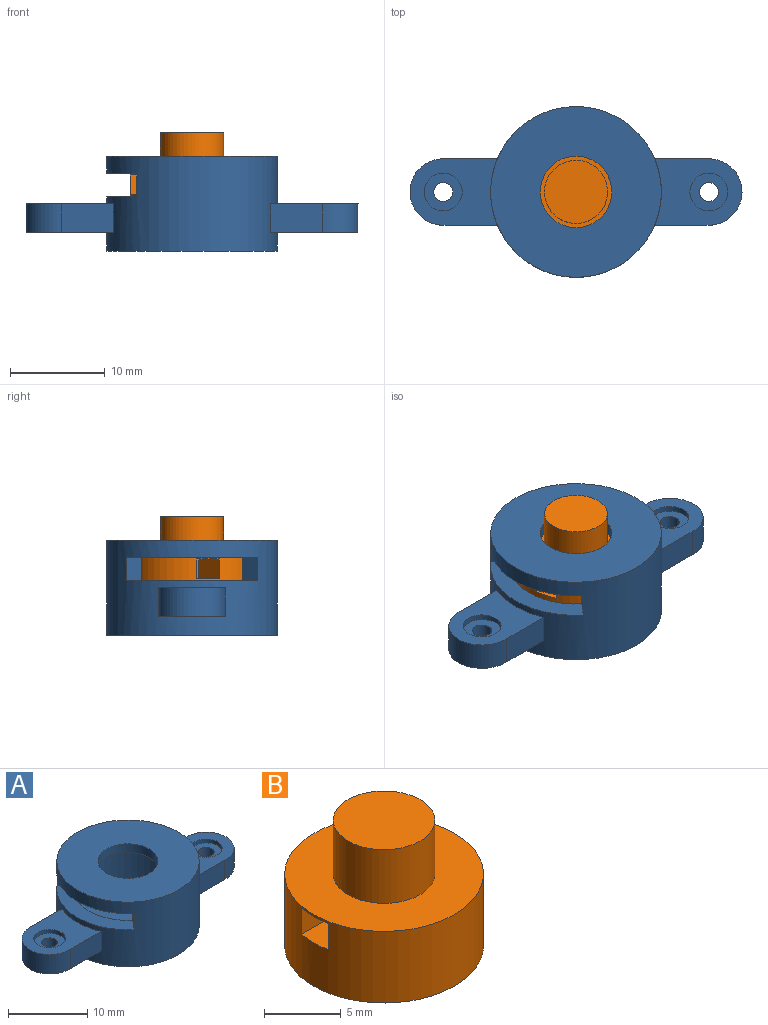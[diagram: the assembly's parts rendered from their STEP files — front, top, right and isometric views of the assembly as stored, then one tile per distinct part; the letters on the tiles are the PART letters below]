
ASSEMBLY  parts=2 mates=1
PART A: 27 faces, bbox 35x18x10 mm
  f0: cylinder r=6.95mm len=13.9mm, axis (0,0,1), area 259.3mm2, adj f5,f6,f23,f24,f25,f26
  f1: cylinder r=3.78mm len=7.55mm, axis (0,0,1), area 31.8mm2, adj f2,f6
  f2: plane 18x18mm, normal (0,0,1), area 209.7mm2, adj f1,f3
  f3: cylinder r=9mm len=18mm, axis (0,0,1), area 483.1mm2, adj f2,f4,f8,f9,f10,f11,f12,f14
  f4: plane 18x18mm, normal (0,0,-1), area 254.5mm2, adj f3
  f5: plane 13.9x13.9mm, normal (0,0,1), area 151.7mm2, adj f0
  f6: plane 13.9x13.9mm, normal (0,0,-1), area 107mm2, adj f0,f1
  f7: cylinder r=3.5mm len=7mm, axis (0,0,1), area 33.9mm2, adj f8,f9,f10,f11
  f8: plane 5.51x3mm, normal (0,-1,0), area 16.5mm2, adj f3,f7,f10,f11
  f9: plane 5.59x3mm, normal (0,1,0), area 16.8mm2, adj f3,f7,f10,f11
  f10: plane 9.21x7mm, normal (0,0,-1), area 52.7mm2, adj f3,f7,f8,f9,f20
  f11: plane 9.21x7mm, normal (0,0,1), area 43.3mm2, adj f3,f7,f8,f9,f22
  f12: plane 5.51x3mm, normal (0,-1,0), area 16.5mm2, adj f3,f13,f15,f16
  f13: cylinder r=3.5mm len=7mm, axis (0,0,1), area 33.9mm2, adj f12,f14,f15,f16
  f14: plane 5.59x3mm, normal (0,1,0), area 16.8mm2, adj f3,f13,f15,f16
  f15: plane 9.21x7mm, normal (0,0,-1), area 52.7mm2, adj f3,f12,f13,f14,f17
  f16: plane 9.21x7mm, normal (0,0,1), area 43.3mm2, adj f3,f12,f13,f14,f19
  f17: cylinder r=1mm len=2.4mm, axis (0,0,1), area 15.1mm2, adj f15,f18
  f18: plane 4x4mm, normal (0,0,1), area 9.4mm2, adj f17,f19
  f19: cylinder r=2mm len=4mm, axis (0,0,1), area 7.5mm2, adj f16,f18
  f20: cylinder r=1mm len=2.4mm, axis (0,0,1), area 15.1mm2, adj f10,f21
  f21: plane 4x4mm, normal (0,0,1), area 9.4mm2, adj f20,f22
  f22: cylinder r=2mm len=4mm, axis (0,0,1), area 7.5mm2, adj f11,f21
  f23: plane 13.81x4.56mm, normal (0,0,-1), area 28.6mm2, adj f0,f3,f25,f26
  f24: plane 13.81x4.56mm, normal (0,0,1), area 28.6mm2, adj f0,f3,f25,f26
  f25: plane 2.51x1.58mm, normal (-0.77,-0.64,0), area 5.1mm2, adj f0,f3,f23,f24
  f26: plane 2.51x1.58mm, normal (-0.77,0.64,0), area 5.1mm2, adj f0,f3,f23,f24
PART B: 10 faces, bbox 13x13x10 mm
  f0: cylinder r=3.32mm len=6.65mm, axis (0,0,1), area 89.7mm2, adj f1,f4
  f1: plane 13x13mm, normal (0,0,1), area 98mm2, adj f0,f2
  f2: cylinder r=6.5mm len=13mm, axis (0,0,1), area 228.8mm2, adj f1,f3,f5,f6,f8,f9
  f3: plane 13x13mm, normal (0,0,-1), area 132.7mm2, adj f2
  f4: plane 6.65x6.65mm, normal (0,0,1), area 34.7mm2, adj f0
  f5: plane 8.47x2.5mm, normal (0,0,-1), area 21.1mm2, adj f2,f7,f8,f9
  f6: plane 8.47x2.5mm, normal (0,0,1), area 21.1mm2, adj f2,f7,f8,f9
  f7: plane 2.5x2.1mm, normal (-1,0,0), area 5.3mm2, adj f5,f6,f8,f9
  f8: plane 8.35x2.1mm, normal (0,1,0), area 17.5mm2, adj f2,f5,f6,f7
  f9: plane 8.35x2.1mm, normal (0,-1,0), area 17.5mm2, adj f2,f5,f6,f7
PLACE A rot(axis=(0.08,0.44,-0.9),0deg) t=(3.46,1.03,-2.12)mm
PLACE B rot(axis=(0,0,1),15deg) t=(3.46,1.03,-2.12)mm
MATE revolute B.f0 <-> A.f0  axis (0,0,1) through (3.46,1.03,5.38)mm
